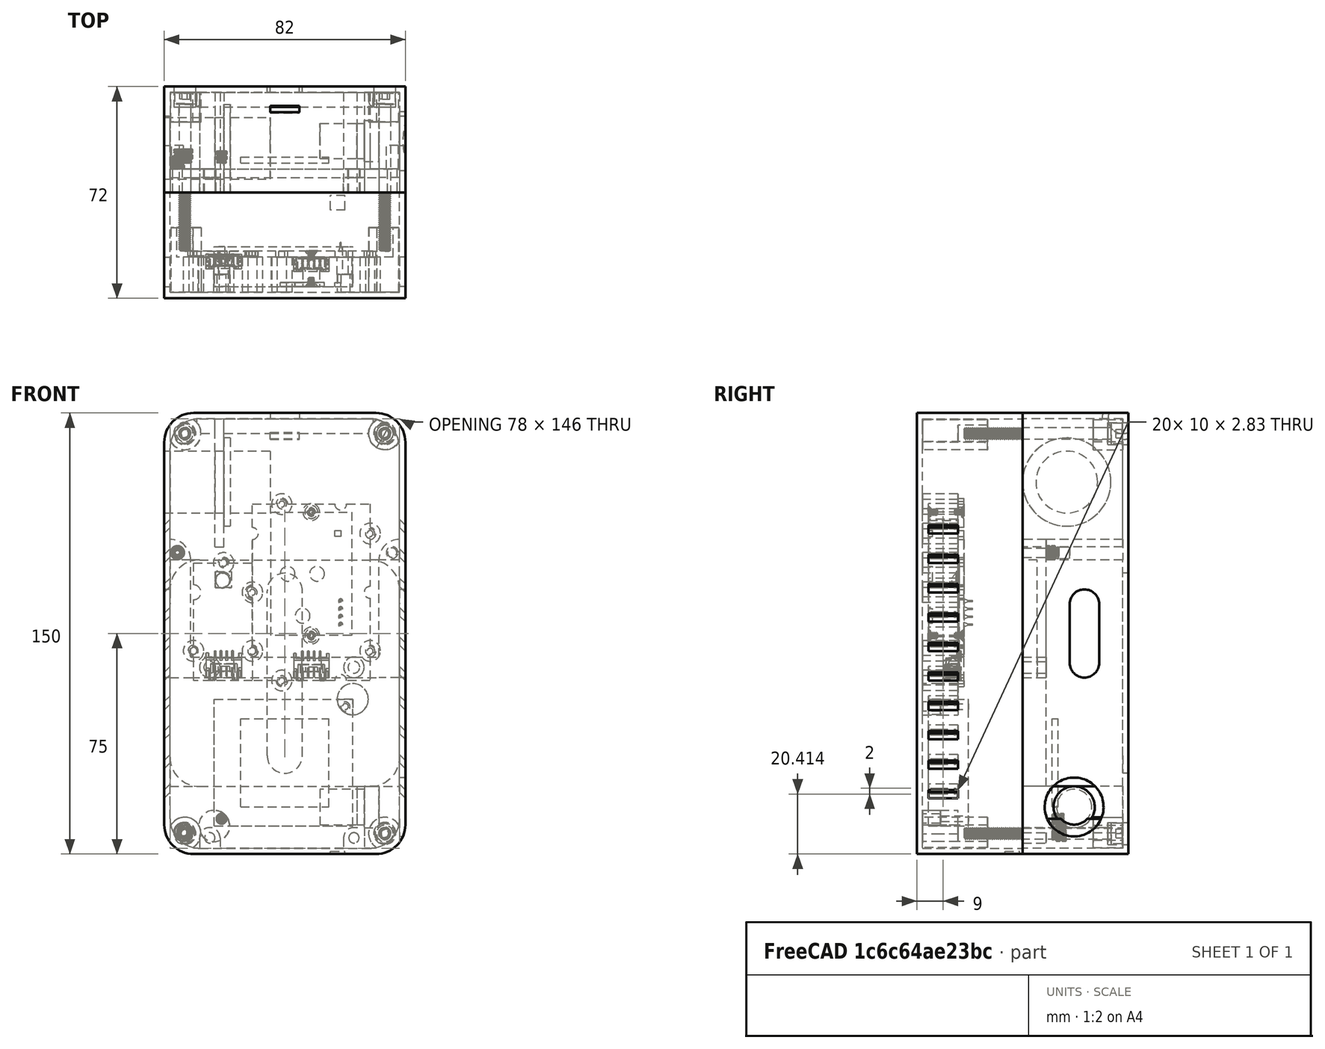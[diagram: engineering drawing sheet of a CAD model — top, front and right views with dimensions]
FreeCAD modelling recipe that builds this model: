
FCSTD DOCUMENT  (FreeCAD 0.20R29177 +233 (Git))
Label: wearableCad_10_11_2022
License: All rights reserved
LicenseURL: http://en.wikipedia.org/wiki/All_rights_reserved
objects: Part::Cylinder×103, Part::Box×65, Part::Cut×53, Part::MultiFuse×39, Part::Feature×10, Part::FeaturePython×1, Mesh::Feature×1
note: 271 computed .brp shape members not serialized (recipe doc carries the construction recipe); baked Part::Feature solids carry a one-line shape summary decoded from their .brp

FEATURE [Part::Feature] Feature  label="Odroid-C4"
  Placement = pos=(66,-10,0) rot=(0.57735,-0.57735,0.57735;2.0944rad)
  shape: bbox 57.1 x 20.65 x 89.5 mm, 2775 faces, 0 solids (baked)
FEATURE [Part::Feature] Feature001  label="SCD30"
  Placement = pos=(-1.3e-14,-22,57) rot=(0,-1,0;1.5708rad)
  shape: bbox 44 x 15.1 x 64 mm, 422 faces, 13 solids (baked)
FEATURE [Part::Feature] Feature002  label="bme280"
  Placement = pos=(-60,-20,58) rot=(0.707107,0,0.707107;3.14159rad)
  shape: bbox 23.8 x 6.016 x 41.9 mm, 221 faces, 2 solids (baked)
FEATURE [Part::MultiFuse] Fusion  label="i2cSensors"
  Placement = pos=(68,-10,0) rot=(0,0,1;0rad)
  Shapes = -> [Feature001,Feature002]
FEATURE [Part::Box] Box  label="ips7100"
  AttacherType = Attacher::AttachEngine3D
  Height = 43.1
  Length = 47.1
  Width = 13.55
FEATURE [Part::Cylinder] Cylinder
  Angle = 360
  AttacherType = Attacher::AttachEngine3D
  FirstAngle = 0
  Height = 13.55
  Placement = pos=(2.5,13.55,2.5) rot=(1,0,0;1.5708rad)
  Radius = 1
  SecondAngle = 0
FEATURE [Part::Cylinder] Cylinder001  label="semiCut"
  Angle = 90
  AttacherType = Attacher::AttachEngine3D
  FirstAngle = 0
  Height = 4.13
  Placement = pos=(0,4.13,-9e-16) rot=(1,0,0;1.5708rad)
  Radius = 5.25
  SecondAngle = 0
FEATURE [Part::MultiFuse] Fusion001  label="ipsCut"
  Shapes = -> [Cylinder,Cylinder001]
FEATURE [Part::Cylinder] Cylinder002
  Angle = 360
  AttacherType = Attacher::AttachEngine3D
  FirstAngle = 0
  Height = 13.55
  Placement = pos=(2.5,13.55,2.5) rot=(1,0,0;1.5708rad)
  Radius = 1
  SecondAngle = 0
FEATURE [Part::Cylinder] Cylinder003  label="semiCut001"
  Angle = 90
  AttacherType = Attacher::AttachEngine3D
  FirstAngle = 0
  Height = 4.13
  Placement = pos=(0,4.13,-9e-16) rot=(1,0,0;1.5708rad)
  Radius = 5.25
  SecondAngle = 0
FEATURE [Part::MultiFuse] Fusion002  label="ipsCut001"
  Placement = pos=(47.1,0,43.1) rot=(0,1,0;3.14159rad)
  Shapes = -> [Cylinder002,Cylinder003]
FEATURE [Part::MultiFuse] Fusion003
  Shapes = -> [Fusion001,Fusion002]
FEATURE [Part::Cut] Cut  label="ips7100V"
  Base = -> Box
  Placement = pos=(15,-42,7.55) rot=(0,0,1;0rad)
  Tool = -> Fusion003
FEATURE [Part::Box] Box001  label="V25B"
  AttacherType = Attacher::AttachEngine3D
  Height = 77
  Length = 78
  Width = 26
FEATURE [Part::Cylinder] Cylinder004
  Angle = 90
  AttacherType = Attacher::AttachEngine3D
  FirstAngle = 0
  Height = 26
  Placement = pos=(0,26,-5.8e-15) rot=(1,0,0;1.5708rad)
  Radius = 10
  SecondAngle = 0
FEATURE [Part::Box] Box002  label="Cube"
  AttacherType = Attacher::AttachEngine3D
  Height = 10
  Length = 10
  Width = 26
FEATURE [Part::Cut] Cut001
  Base = -> Box002
  Placement = pos=(68,0,67) rot=(0,0,1;0rad)
  Tool = -> Cylinder004
FEATURE [Part::Box] Box003  label="Cube001"
  AttacherType = Attacher::AttachEngine3D
  Height = 10
  Length = 10
  Width = 26
FEATURE [Part::Cylinder] Cylinder005
  Angle = 90
  AttacherType = Attacher::AttachEngine3D
  FirstAngle = 0
  Height = 26
  Placement = pos=(0,26,-5.8e-15) rot=(1,0,0;1.5708rad)
  Radius = 10
  SecondAngle = 0
FEATURE [Part::Cut] Cut002
  Base = -> Box003
  Placement = pos=(68,0,10) rot=(0,1,0;1.5708rad)
  Tool = -> Cylinder005
FEATURE [Part::Box] Box004  label="Cube002"
  AttacherType = Attacher::AttachEngine3D
  Height = 10
  Length = 10
  Width = 26
FEATURE [Part::Cylinder] Cylinder006
  Angle = 90
  AttacherType = Attacher::AttachEngine3D
  FirstAngle = 0
  Height = 26
  Placement = pos=(0,26,-5.8e-15) rot=(1,0,0;1.5708rad)
  Radius = 10
  SecondAngle = 0
FEATURE [Part::Cut] Cut003
  Base = -> Box004
  Placement = pos=(10,0,10) rot=(0,1,0;3.14159rad)
  Tool = -> Cylinder006
FEATURE [Part::Box] Box005  label="Cube003"
  AttacherType = Attacher::AttachEngine3D
  Height = 10
  Length = 10
  Width = 26
FEATURE [Part::Cylinder] Cylinder007
  Angle = 90
  AttacherType = Attacher::AttachEngine3D
  FirstAngle = 0
  Height = 26
  Placement = pos=(0,26,-5.8e-15) rot=(1,0,0;1.5708rad)
  Radius = 10
  SecondAngle = 0
FEATURE [Part::Cut] Cut004
  Base = -> Box005
  Placement = pos=(10,0,67) rot=(0,-1,0;1.5708rad)
  Tool = -> Cylinder007
FEATURE [Part::MultiFuse] Fusion004  label="v25Cuts"
  Shapes = -> [Cut001,Cut002,Cut003,Cut004]
FEATURE [Part::Cut] Cut005  label="V25B001"
  Base = -> Box001
  Placement = pos=(0,-2,21) rot=(0,0,1;0rad)
  Tool = -> Fusion004
FEATURE [Part::Box] Box007  label="Cube004"
  AttacherType = Attacher::AttachEngine3D
  Height = 10
  Length = 10
  Placement = pos=(0,-10,0) rot=(0,0,1;0rad)
  Width = 36
FEATURE [Part::Cylinder] Cylinder008
  Angle = 90
  AttacherType = Attacher::AttachEngine3D
  FirstAngle = 0
  Height = 36
  Placement = pos=(0,26,-5.8e-15) rot=(1,0,0;1.5708rad)
  Radius = 10
  SecondAngle = 0
FEATURE [Part::Cut] Cut006
  Base = -> Box007
  Placement = pos=(8,18,8) rot=(0.707107,0,-0.707107;3.14159rad)
  Tool = -> Cylinder008
FEATURE [Part::Box] Box008  label="baseOut001"
  AttacherType = Attacher::AttachEngine3D
  Height = 150
  Length = 82
  Placement = pos=(80,26,-2) rot=(0,0,1;3.14159rad)
  Width = 36
FEATURE [Part::Box] Box009  label="Cube005"
  AttacherType = Attacher::AttachEngine3D
  Height = 10
  Length = 10
  Placement = pos=(0,-10,0) rot=(0,0,1;0rad)
  Width = 36
FEATURE [Part::Cylinder] Cylinder009
  Angle = 90
  AttacherType = Attacher::AttachEngine3D
  FirstAngle = 0
  Height = 36
  Placement = pos=(0,26,-5.8e-15) rot=(1,0,0;1.5708rad)
  Radius = 10
  SecondAngle = 0
FEATURE [Part::Cut] Cut007
  Base = -> Box009
  Placement = pos=(70,18,8) rot=(1,0,0;3.14159rad)
  Tool = -> Cylinder009
FEATURE [Part::Box] Box010  label="Cube006"
  AttacherType = Attacher::AttachEngine3D
  Height = 10
  Length = 10
  Placement = pos=(0,-10,0) rot=(0,0,1;0rad)
  Width = 36
FEATURE [Part::Cylinder] Cylinder010
  Angle = 90
  AttacherType = Attacher::AttachEngine3D
  FirstAngle = 0
  Height = 36
  Placement = pos=(0,26,-5.8e-15) rot=(1,0,0;1.5708rad)
  Radius = 10
  SecondAngle = 0
FEATURE [Part::Cut] Cut008
  Base = -> Box010
  Placement = pos=(8,18,138) rot=(0,0,1;3.14159rad)
  Tool = -> Cylinder010
FEATURE [Part::Box] Box011  label="Cube007"
  AttacherType = Attacher::AttachEngine3D
  Height = 10
  Length = 10
  Placement = pos=(0,-10,0) rot=(0,0,1;0rad)
  Width = 36
FEATURE [Part::Cylinder] Cylinder011
  Angle = 90
  AttacherType = Attacher::AttachEngine3D
  FirstAngle = 0
  Height = 36
  Placement = pos=(0,26,-5.8e-15) rot=(1,0,0;1.5708rad)
  Radius = 10
  SecondAngle = 0
FEATURE [Part::Cut] Cut009
  Base = -> Box011
  Placement = pos=(70,18,138) rot=(0.707107,0,0.707107;3.14159rad)
  Tool = -> Cylinder011
FEATURE [Part::MultiFuse] Fusion005
  Placement = pos=(0,-2,0) rot=(0,0,1;0rad)
  Shapes = -> [Cut006,Cut007,Cut008,Cut009]
FEATURE [Part::Cut] Cut010  label="BaseOut"
  Base = -> Box008
  Tool = -> Fusion005
FEATURE [Part::Box] Box013  label="Cube009"
  AttacherType = Attacher::AttachEngine3D
  Height = 10
  Length = 10
  Placement = pos=(0,-8,0) rot=(0,0,1;0rad)
  Width = 34
FEATURE [Part::Box] Box014  label="baseOut002"
  AttacherType = Attacher::AttachEngine3D
  Height = 146
  Length = 78
  Placement = pos=(80,26,-2) rot=(0,0,1;3.14159rad)
  Width = 34
FEATURE [Part::Box] Box015  label="Cube010"
  AttacherType = Attacher::AttachEngine3D
  Height = 10
  Length = 10
  Placement = pos=(0,-8,0) rot=(0,0,1;0rad)
  Width = 34
FEATURE [Part::Box] Box016  label="Cube011"
  AttacherType = Attacher::AttachEngine3D
  Height = 10
  Length = 10
  Placement = pos=(0,-8,0) rot=(0,0,1;0rad)
  Width = 34
FEATURE [Part::Box] Box017  label="Cube012"
  AttacherType = Attacher::AttachEngine3D
  Height = 10
  Length = 10
  Placement = pos=(0,-8,0) rot=(0,0,1;0rad)
  Width = 34
FEATURE [Part::Cylinder] Cylinder013
  Angle = 90
  AttacherType = Attacher::AttachEngine3D
  FirstAngle = 0
  Height = 34
  Placement = pos=(0,26,-5.8e-15) rot=(1,0,0;1.5708rad)
  Radius = 10
  SecondAngle = 0
FEATURE [Part::Cut] Cut012
  Base = -> Box013
  Placement = pos=(12,18,8) rot=(0.707107,0,-0.707107;3.14159rad)
  Tool = -> Cylinder013
FEATURE [Part::Cylinder] Cylinder014
  Angle = 90
  AttacherType = Attacher::AttachEngine3D
  FirstAngle = 0
  Height = 34
  Placement = pos=(0,26,-5.8e-15) rot=(1,0,0;1.5708rad)
  Radius = 10
  SecondAngle = 0
FEATURE [Part::Cut] Cut013
  Base = -> Box015
  Placement = pos=(70,18,8) rot=(1,0,0;3.14159rad)
  Tool = -> Cylinder014
FEATURE [Part::Cylinder] Cylinder015
  Angle = 90
  AttacherType = Attacher::AttachEngine3D
  FirstAngle = 0
  Height = 34
  Placement = pos=(0,26,-5.8e-15) rot=(1,0,0;1.5708rad)
  Radius = 10
  SecondAngle = 0
FEATURE [Part::Cut] Cut014
  Base = -> Box016
  Placement = pos=(12,18,134) rot=(0,0,1;3.14159rad)
  Tool = -> Cylinder015
FEATURE [Part::Cylinder] Cylinder016
  Angle = 90
  AttacherType = Attacher::AttachEngine3D
  FirstAngle = 0
  Height = 34
  Placement = pos=(0,26,-5.8e-15) rot=(1,0,0;1.5708rad)
  Radius = 10
  SecondAngle = 0
FEATURE [Part::Cut] Cut015
  Base = -> Box017
  Placement = pos=(70,18,134) rot=(0.707107,0,0.707107;3.14159rad)
  Tool = -> Cylinder016
FEATURE [Part::MultiFuse] Fusion006
  Shapes = -> [Cut012,Cut013,Cut014,Cut015]
FEATURE [Part::Cut] Cut016  label="BaseOut001"
  Base = -> Box014
  Placement = pos=(-2,-2,2) rot=(0,0,1;0rad)
  Tool = -> Fusion006
FEATURE [Part::Cut] Cut017  label="baseOut"
  Base = -> Cut010
  Tool = -> Cut016
FEATURE [Part::Box] Box018  label="Cube013"
  AttacherType = Attacher::AttachEngine3D
  Height = 10
  Length = 10
  Placement = pos=(10,26,0) rot=(0,0,1;3.14159rad)
  Width = 26
FEATURE [Part::Cylinder] Cylinder017
  Angle = 90
  AttacherType = Attacher::AttachEngine3D
  FirstAngle = 0
  Height = 26
  Placement = pos=(0,26,-5.8e-15) rot=(1,0,0;1.5708rad)
  Radius = 10
  SecondAngle = 0
FEATURE [Part::Cut] Cut018  label="batterySupport"
  Base = -> Box018
  Placement = pos=(10,-2,31) rot=(0,1,0;3.14159rad)
  Tool = -> Cylinder017
FEATURE [Part::Box] Box019  label="Cube014"
  AttacherType = Attacher::AttachEngine3D
  Height = 10
  Length = 10
  Placement = pos=(10,26,0) rot=(0,0,1;3.14159rad)
  Width = 26
FEATURE [Part::Cylinder] Cylinder018
  Angle = 90
  AttacherType = Attacher::AttachEngine3D
  FirstAngle = 0
  Height = 26
  Placement = pos=(0,26,-5.8e-15) rot=(1,0,0;1.5708rad)
  Radius = 10
  SecondAngle = 0
FEATURE [Part::Cut] Cut019  label="batterySupport001"
  Base = -> Box019
  Placement = pos=(68,-2,31) rot=(0,1,0;1.5708rad)
  Tool = -> Cylinder018
FEATURE [Part::Box] Box020  label="Cube015"
  AttacherType = Attacher::AttachEngine3D
  Height = 10
  Length = 10
  Placement = pos=(10,26,0) rot=(0,0,1;3.14159rad)
  Width = 26
FEATURE [Part::Cylinder] Cylinder019
  Angle = 90
  AttacherType = Attacher::AttachEngine3D
  FirstAngle = 0
  Height = 26
  Placement = pos=(0,26,-5.8e-15) rot=(1,0,0;1.5708rad)
  Radius = 10
  SecondAngle = 0
FEATURE [Part::Cut] Cut020  label="batterySupport002"
  Base = -> Box020
  Placement = pos=(68,-2,88) rot=(0,0,1;0rad)
  Tool = -> Cylinder019
FEATURE [Part::Box] Box021  label="Cube016"
  AttacherType = Attacher::AttachEngine3D
  Height = 10
  Length = 10
  Placement = pos=(10,26,0) rot=(0,0,1;3.14159rad)
  Width = 26
FEATURE [Part::Cylinder] Cylinder020
  Angle = 90
  AttacherType = Attacher::AttachEngine3D
  FirstAngle = 0
  Height = 26
  Placement = pos=(0,26,-5.8e-15) rot=(1,0,0;1.5708rad)
  Radius = 10
  SecondAngle = 0
FEATURE [Part::Cut] Cut021  label="batterySupport003"
  Base = -> Box021
  Placement = pos=(10,-2,88) rot=(0,-1,0;1.5708rad)
  Tool = -> Cylinder020
FEATURE [Part::Cylinder] Cylinder021
  Angle = 360
  AttacherType = Attacher::AttachEngine3D
  FirstAngle = 0
  Height = 34
  Placement = pos=(13.5,24,3.5) rot=(1,0,0;1.5708rad)
  Radius = 3.5
  SecondAngle = 0
FEATURE [Part::Cylinder] Cylinder022
  Angle = 360
  AttacherType = Attacher::AttachEngine3D
  FirstAngle = 0
  Height = 8
  Placement = pos=(13.5,-2,3.5) rot=(1,0,0;1.5708rad)
  Radius = 1.75
  SecondAngle = 0
FEATURE [Part::Box] Box022  label="Cube017"
  AttacherType = Attacher::AttachEngine3D
  Height = 3.5
  Length = 7
  Placement = pos=(10,24,3.5) rot=(1,0,0;3.14159rad)
  Width = 34
FEATURE [Part::Cylinder] Cylinder023
  Angle = 360
  AttacherType = Attacher::AttachEngine3D
  FirstAngle = 0
  Height = 34
  Placement = pos=(62.5,24,3.5) rot=(1,0,0;1.5708rad)
  Radius = 3.5
  SecondAngle = 0
FEATURE [Part::Cylinder] Cylinder024
  Angle = 360
  AttacherType = Attacher::AttachEngine3D
  FirstAngle = 0
  Height = 8
  Placement = pos=(62.5,-2,3.5) rot=(1,0,0;1.5708rad)
  Radius = 1.75
  SecondAngle = 0
FEATURE [Part::Box] Box023  label="Cube018"
  AttacherType = Attacher::AttachEngine3D
  Height = 3.5
  Length = 7
  Placement = pos=(59,24,3.5) rot=(1,0,0;3.14159rad)
  Width = 34
FEATURE [Part::Cylinder] Cylinder025
  Angle = 360
  AttacherType = Attacher::AttachEngine3D
  FirstAngle = 0
  Height = 20
  Radius = 6
  SecondAngle = 0
FEATURE [Part::Cylinder] Cylinder026
  Angle = 360
  AttacherType = Attacher::AttachEngine3D
  FirstAngle = 0
  Height = 5
  Radius = 7
  SecondAngle = 0
FEATURE [Part::MultiFuse] Fusion007  label="powerSwitch"
  Placement = pos=(71,7.5,14) rot=(0,-1,0;1.5708rad)
  Shapes = -> [Cylinder025,Cylinder026]
FEATURE [Part::Box] Box024  label="Cube019"
  AttacherType = Attacher::AttachEngine3D
  Height = 17.5
  Length = 2.5
  Placement = pos=(63.5,24,21) rot=(1,0,0;3.14159rad)
  Width = 34
FEATURE [Part::MultiFuse] Fusion008  label="base"
  Shapes = -> [Cut017,Cut018,Cut019,Cut020,Cut021]
FEATURE [Part::MultiFuse] Fusion009  label="base001"
  Shapes = -> [Cylinder021,Cylinder023,Box022,Box023,Box024,Fusion008]
FEATURE [Part::MultiFuse] Fusion010  label="baseCuts"
  Shapes = -> [Cylinder024,Cylinder022,Fusion007]
FEATURE [Part::Cut] Cut022  label="base002"
  Base = -> Fusion009
  Tool = -> Fusion010
FEATURE [Part::Cylinder] Cylinder027  label="mainMounts"
  Angle = 90
  AttacherType = Attacher::AttachEngine3D
  FirstAngle = 0
  Height = 26
  Placement = pos=(0,24,98) rot=(1,0,0;1.5708rad)
  Radius = 7
  SecondAngle = 0
FEATURE [Part::Cylinder] Cylinder028  label="mainMounts001"
  Angle = 90
  AttacherType = Attacher::AttachEngine3D
  FirstAngle = 0
  Height = 26
  Placement = pos=(78,24,98) rot=(0.57735,-0.57735,0.57735;2.0944rad)
  Radius = 7
  SecondAngle = 0
FEATURE [Part::Cylinder] Cylinder029
  Angle = 360
  AttacherType = Attacher::AttachEngine3D
  FirstAngle = 0
  Height = 8
  Placement = pos=(2.5,-2,100.5) rot=(1,0,0;1.5708rad)
  Radius = 2
  SecondAngle = 0
FEATURE [Part::Cylinder] Cylinder030
  Angle = 360
  AttacherType = Attacher::AttachEngine3D
  FirstAngle = 0
  Height = 8
  Placement = pos=(75.5,-2,100.5) rot=(1,0,0;1.5708rad)
  Radius = 2
  SecondAngle = 0
FEATURE [Part::MultiFuse] Fusion011  label="baseCuts001"
  Placement = pos=(0,8,0) rot=(0,0,1;0rad)
  Shapes = -> [Cylinder029,Cylinder030]
FEATURE [Part::MultiFuse] Fusion012
  Shapes = -> [Cylinder028,Cylinder027]
FEATURE [Part::MultiFuse] Fusion013  label="base003"
  Shapes = -> [Cut022,Fusion012]
FEATURE [Part::Cut] Cut023  label="baseBottom"
  Base = -> Fusion013
  Tool = -> Fusion011
FEATURE [Part::Feature] Solid  label="m3HeatSet"
  Placement = pos=(2.5,2.3,100.5) rot=(1,0,0;3.14159rad)
  shape: bbox 4.772 x 4.354 x 4.772 mm, 239 faces (baked)
FEATURE [Part::Cylinder] Cylinder031
  Angle = 360
  AttacherType = Attacher::AttachEngine3D
  FirstAngle = 0
  Height = 8
  Placement = pos=(13.5,-2,61.5) rot=(1,0,0;1.5708rad)
  Radius = 3.5
  SecondAngle = 0
FEATURE [Part::Cylinder] Cylinder032  label="cuts"
  Angle = 360
  AttacherType = Attacher::AttachEngine3D
  FirstAngle = 0
  Height = 8
  Placement = pos=(13.5,-2,61.5) rot=(1,0,0;1.5708rad)
  Radius = 2
  SecondAngle = 0
FEATURE [Part::Cylinder] Cylinder034
  Angle = 360
  AttacherType = Attacher::AttachEngine3D
  FirstAngle = 0
  Height = 8
  Placement = pos=(62.5,-2,61.5) rot=(1,0,0;1.5708rad)
  Radius = 3.5
  SecondAngle = 0
FEATURE [Part::Cylinder] Cylinder035  label="cuts001"
  Angle = 360
  AttacherType = Attacher::AttachEngine3D
  FirstAngle = 0
  Height = 8
  Placement = pos=(62.5,-2,61.5) rot=(1,0,0;1.5708rad)
  Radius = 2
  SecondAngle = 0
FEATURE [Part::Cylinder] Cylinder036
  Angle = 90
  AttacherType = Attacher::AttachEngine3D
  FirstAngle = 0
  Height = 8
  Placement = pos=(78,-2,98) rot=(0.57735,-0.57735,0.57735;2.0944rad)
  Radius = 7
  SecondAngle = 0
FEATURE [Part::Cylinder] Cylinder037
  Angle = 90
  AttacherType = Attacher::AttachEngine3D
  FirstAngle = 0
  Height = 8
  Placement = pos=(0,-2,98) rot=(1,0,0;1.5708rad)
  Radius = 7
  SecondAngle = 0
FEATURE [Part::Box] Box025  label="Cube020"
  AttacherType = Attacher::AttachEngine3D
  Height = 7
  Length = 78
  Placement = pos=(0,-5,58) rot=(0,0,1;0rad)
  Width = 3
FEATURE [Part::Box] Box026  label="Cube021"
  AttacherType = Attacher::AttachEngine3D
  Height = 7
  Length = 40
  Placement = pos=(7,-5,58) rot=(0,-1,0;1.5708rad)
  Width = 3
FEATURE [Part::Box] Box027  label="Cube022"
  AttacherType = Attacher::AttachEngine3D
  Height = 7
  Length = 40
  Placement = pos=(78,-5,58) rot=(0,-1,0;1.5708rad)
  Width = 3
FEATURE [Part::MultiFuse] Fusion014
  Shapes = -> [Box027,Box025,Box026,Cylinder034,Cylinder031]
FEATURE [Part::Cylinder] Cylinder038  label="m3Screw"
  Angle = 360
  AttacherType = Attacher::AttachEngine3D
  FirstAngle = 0
  Height = 8
  Placement = pos=(75.5,-2,100.5) rot=(1,0,0;1.5708rad)
  Radius = 1.6
  SecondAngle = 0
FEATURE [Part::Cylinder] Cylinder039  label="m3Screw001"
  Angle = 360
  AttacherType = Attacher::AttachEngine3D
  FirstAngle = 0
  Height = 8
  Placement = pos=(2.5,-2,100.5) rot=(1,0,0;1.5708rad)
  Radius = 1.6
  SecondAngle = 0
FEATURE [Part::MultiFuse] Fusion015  label="c4Hold"
  Shapes = -> [Cylinder036,Cylinder037,Fusion014]
FEATURE [Part::MultiFuse] Fusion016  label="c4oldCuts"
  Shapes = -> [Cylinder039,Cylinder032,Cylinder035,Cylinder038]
FEATURE [Part::Cut] Cut024  label="c4Hold001"
  Base = -> Fusion015
  Tool = -> Fusion016
FEATURE [Part::Box] Box028  label="Cube023"
  AttacherType = Attacher::AttachEngine3D
  Height = 10
  Length = 10
  Placement = pos=(0,-10,0) rot=(0,0,1;0rad)
  Width = 36
FEATURE [Part::Box] Box029  label="baseOut003"
  AttacherType = Attacher::AttachEngine3D
  Height = 150
  Length = 82
  Placement = pos=(80,26,-2) rot=(0,0,1;3.14159rad)
  Width = 36
FEATURE [Part::Box] Box030  label="Cube024"
  AttacherType = Attacher::AttachEngine3D
  Height = 10
  Length = 10
  Placement = pos=(0,-10,0) rot=(0,0,1;0rad)
  Width = 36
FEATURE [Part::Box] Box031  label="Cube025"
  AttacherType = Attacher::AttachEngine3D
  Height = 10
  Length = 10
  Placement = pos=(0,-10,0) rot=(0,0,1;0rad)
  Width = 36
FEATURE [Part::Box] Box032  label="Cube026"
  AttacherType = Attacher::AttachEngine3D
  Height = 10
  Length = 10
  Placement = pos=(0,-10,0) rot=(0,0,1;0rad)
  Width = 36
FEATURE [Part::Box] Box033  label="Cube027"
  AttacherType = Attacher::AttachEngine3D
  Height = 10
  Length = 10
  Placement = pos=(0,-8,0) rot=(0,0,1;0rad)
  Width = 34
FEATURE [Part::Box] Box034  label="baseOut004"
  AttacherType = Attacher::AttachEngine3D
  Height = 146
  Length = 78
  Placement = pos=(80,26,-2) rot=(0,0,1;3.14159rad)
  Width = 34
FEATURE [Part::Box] Box035  label="Cube028"
  AttacherType = Attacher::AttachEngine3D
  Height = 10
  Length = 10
  Placement = pos=(0,-8,0) rot=(0,0,1;0rad)
  Width = 34
FEATURE [Part::Box] Box036  label="Cube029"
  AttacherType = Attacher::AttachEngine3D
  Height = 10
  Length = 10
  Placement = pos=(0,-8,0) rot=(0,0,1;0rad)
  Width = 34
FEATURE [Part::Box] Box037  label="Cube030"
  AttacherType = Attacher::AttachEngine3D
  Height = 10
  Length = 10
  Placement = pos=(0,-8,0) rot=(0,0,1;0rad)
  Width = 34
FEATURE [Part::Cylinder] Cylinder040
  Angle = 90
  AttacherType = Attacher::AttachEngine3D
  FirstAngle = 0
  Height = 36
  Placement = pos=(0,26,-5.8e-15) rot=(1,0,0;1.5708rad)
  Radius = 10
  SecondAngle = 0
FEATURE [Part::Cut] Cut025
  Base = -> Box028
  Placement = pos=(8,18,8) rot=(0.707107,0,-0.707107;3.14159rad)
  Tool = -> Cylinder040
FEATURE [Part::Cylinder] Cylinder041
  Angle = 90
  AttacherType = Attacher::AttachEngine3D
  FirstAngle = 0
  Height = 36
  Placement = pos=(0,26,-5.8e-15) rot=(1,0,0;1.5708rad)
  Radius = 10
  SecondAngle = 0
FEATURE [Part::Cut] Cut026
  Base = -> Box030
  Placement = pos=(70,18,8) rot=(1,0,0;3.14159rad)
  Tool = -> Cylinder041
FEATURE [Part::Cylinder] Cylinder042
  Angle = 90
  AttacherType = Attacher::AttachEngine3D
  FirstAngle = 0
  Height = 36
  Placement = pos=(0,26,-5.8e-15) rot=(1,0,0;1.5708rad)
  Radius = 10
  SecondAngle = 0
FEATURE [Part::Cut] Cut027
  Base = -> Box031
  Placement = pos=(8,18,138) rot=(0,0,1;3.14159rad)
  Tool = -> Cylinder042
FEATURE [Part::Cylinder] Cylinder043
  Angle = 90
  AttacherType = Attacher::AttachEngine3D
  FirstAngle = 0
  Height = 36
  Placement = pos=(0,26,-5.8e-15) rot=(1,0,0;1.5708rad)
  Radius = 10
  SecondAngle = 0
FEATURE [Part::Cut] Cut028
  Base = -> Box032
  Placement = pos=(70,18,138) rot=(0.707107,0,0.707107;3.14159rad)
  Tool = -> Cylinder043
FEATURE [Part::Cylinder] Cylinder044
  Angle = 90
  AttacherType = Attacher::AttachEngine3D
  FirstAngle = 0
  Height = 34
  Placement = pos=(0,26,-5.8e-15) rot=(1,0,0;1.5708rad)
  Radius = 10
  SecondAngle = 0
FEATURE [Part::Cut] Cut030
  Base = -> Box033
  Placement = pos=(12,18,8) rot=(0.707107,0,-0.707107;3.14159rad)
  Tool = -> Cylinder044
FEATURE [Part::Cylinder] Cylinder045
  Angle = 90
  AttacherType = Attacher::AttachEngine3D
  FirstAngle = 0
  Height = 34
  Placement = pos=(0,26,-5.8e-15) rot=(1,0,0;1.5708rad)
  Radius = 10
  SecondAngle = 0
FEATURE [Part::Cut] Cut031
  Base = -> Box035
  Placement = pos=(70,18,8) rot=(1,0,0;3.14159rad)
  Tool = -> Cylinder045
FEATURE [Part::Cylinder] Cylinder046
  Angle = 90
  AttacherType = Attacher::AttachEngine3D
  FirstAngle = 0
  Height = 34
  Placement = pos=(0,26,-5.8e-15) rot=(1,0,0;1.5708rad)
  Radius = 10
  SecondAngle = 0
FEATURE [Part::Cut] Cut032
  Base = -> Box036
  Placement = pos=(12,18,134) rot=(0,0,1;3.14159rad)
  Tool = -> Cylinder046
FEATURE [Part::Cylinder] Cylinder047
  Angle = 90
  AttacherType = Attacher::AttachEngine3D
  FirstAngle = 0
  Height = 34
  Placement = pos=(0,26,-5.8e-15) rot=(1,0,0;1.5708rad)
  Radius = 10
  SecondAngle = 0
FEATURE [Part::Cut] Cut033
  Base = -> Box037
  Placement = pos=(70,18,134) rot=(0.707107,0,0.707107;3.14159rad)
  Tool = -> Cylinder047
FEATURE [Part::MultiFuse] Fusion017
  Placement = pos=(0,-2,0) rot=(0,0,1;0rad)
  Shapes = -> [Cut025,Cut026,Cut027,Cut028]
FEATURE [Part::Cut] Cut029  label="BaseOut002"
  Base = -> Box029
  Tool = -> Fusion017
FEATURE [Part::MultiFuse] Fusion018
  Shapes = -> [Cut030,Cut031,Cut032,Cut033]
FEATURE [Part::Cut] Cut034  label="BaseOut003"
  Base = -> Box034
  Placement = pos=(-2,-2,2) rot=(0,0,1;0rad)
  Tool = -> Fusion018
FEATURE [Part::Cut] Cut035  label="baseTop"
  Base = -> Cut029
  Placement = pos=(78,-20,0) rot=(0,0,1;3.14159rad)
  Tool = -> Cut034
FEATURE [Part::Feature] Solid001  label="m2HeatSet"
  Placement = pos=(17.5,0,10) rot=(0,0,1;0rad)
  shape: bbox 3.655 x 4.083 x 3.655 mm, 239 faces (baked)
FEATURE [Part::Cylinder] Cylinder048
  Angle = 360
  AttacherType = Attacher::AttachEngine3D
  FirstAngle = 0
  Height = 6
  Placement = pos=(17.5,-44,10.05) rot=(-1,0,0;1.5708rad)
  Radius = 1.57
  SecondAngle = 0
FEATURE [Part::Cylinder] Cylinder049
  Angle = 360
  AttacherType = Attacher::AttachEngine3D
  FirstAngle = 0
  Height = 6
  Placement = pos=(15,-44,7.55) rot=(0.57735,0.57735,0.57735;4.18879rad)
  Radius = 5.3
  SecondAngle = 0
FEATURE [Part::Cylinder] Cylinder050
  Angle = 360
  AttacherType = Attacher::AttachEngine3D
  FirstAngle = 0
  Height = 6
  Placement = pos=(62.1,-44,50.65) rot=(0.57735,-0.57735,-0.57735;4.18879rad)
  Radius = 5.3
  SecondAngle = 0
FEATURE [Part::Cylinder] Cylinder051
  Angle = 360
  AttacherType = Attacher::AttachEngine3D
  FirstAngle = 0
  Height = 6
  Placement = pos=(59.6,-44,48.15) rot=(-1,0,0;1.5708rad)
  Radius = 1.57
  SecondAngle = 0
FEATURE [Part::Cut] Cut036
  Base = -> Cylinder049
  Tool = -> Cylinder048
FEATURE [Part::Cut] Cut037
  Base = -> Cylinder050
  Tool = -> Cylinder051
FEATURE [Part::Cylinder] Cylinder052
  Angle = 270
  AttacherType = Attacher::AttachEngine3D
  FirstAngle = 0
  Height = 6
  Placement = pos=(15,-38,7.55) rot=(-1,0,0;1.5708rad)
  Radius = 5.3
  SecondAngle = 0
FEATURE [Part::Cylinder] Cylinder053
  Angle = 270
  AttacherType = Attacher::AttachEngine3D
  FirstAngle = 0
  Height = 6
  Placement = pos=(62.1,-38,50.65) rot=(0,0.707107,0.707107;3.14159rad)
  Radius = 5.3
  SecondAngle = 0
FEATURE [Part::MultiFuse] Fusion019  label="baseTop001"
  Shapes = -> [Cut036,Cut037,Cylinder052,Cylinder053,Cut035]
FEATURE [Part::Cylinder] Cylinder054  label="m2HeatSet001"
  Angle = 360
  AttacherType = Attacher::AttachEngine3D
  FirstAngle = 0
  Height = 12
  Placement = pos=(8,-44,67.1) rot=(-1,0,0;1.5708rad)
  Radius = 1.6
  SecondAngle = 0
FEATURE [Part::Cylinder] Cylinder055  label="m2HeatSet002"
  Angle = 360
  AttacherType = Attacher::AttachEngine3D
  FirstAngle = 0
  Height = 12
  Placement = pos=(28,-44,67.1) rot=(-1,0,0;1.5708rad)
  Radius = 1.6
  SecondAngle = 0
FEATURE [Part::Cylinder] Cylinder056  label="m2HeatSet003"
  Angle = 360
  AttacherType = Attacher::AttachEngine3D
  FirstAngle = 0
  Height = 12
  Placement = pos=(68,-44,67.1) rot=(-1,0,0;1.5708rad)
  Radius = 1.6
  SecondAngle = 0
FEATURE [Part::Cylinder] Cylinder057  label="m2HeatSet004"
  Angle = 360
  AttacherType = Attacher::AttachEngine3D
  FirstAngle = 0
  Height = 12
  Placement = pos=(18.2,-44,97) rot=(-1,0,0;1.5708rad)
  Radius = 1.6
  SecondAngle = 0
FEATURE [Part::Cylinder] Cylinder058  label="m2HeatSet005"
  Angle = 360
  AttacherType = Attacher::AttachEngine3D
  FirstAngle = 0
  Height = 12
  Placement = pos=(28,-44,87) rot=(-1,0,0;1.5708rad)
  Radius = 1.6
  SecondAngle = 0
FEATURE [Part::Cylinder] Cylinder059  label="m2HeatSet006"
  Angle = 360
  AttacherType = Attacher::AttachEngine3D
  FirstAngle = 0
  Height = 12
  Placement = pos=(38,-44,117) rot=(-1,0,0;1.5708rad)
  Radius = 1.6
  SecondAngle = 0
FEATURE [Part::Cylinder] Cylinder060  label="m2HeatSet007"
  Angle = 360
  AttacherType = Attacher::AttachEngine3D
  FirstAngle = 0
  Height = 12
  Placement = pos=(38,-44,57) rot=(-1,0,0;1.5708rad)
  Radius = 1.6
  SecondAngle = 0
FEATURE [Part::Cylinder] Cylinder061  label="m2HeatSet008"
  Angle = 360
  AttacherType = Attacher::AttachEngine3D
  FirstAngle = 0
  Height = 12
  Placement = pos=(68,-44,107) rot=(-1,0,0;1.5708rad)
  Radius = 1.6
  SecondAngle = 0
FEATURE [Part::Cylinder] Cylinder062  label="m2HeatSetOut"
  Angle = 360
  AttacherType = Attacher::AttachEngine3D
  FirstAngle = 0
  Height = 12
  Placement = pos=(8,-44,67.1) rot=(-1,0,0;1.5708rad)
  Radius = 3.5
  SecondAngle = 0
FEATURE [Part::Cylinder] Cylinder063  label="m2HeatSetOut001"
  Angle = 360
  AttacherType = Attacher::AttachEngine3D
  FirstAngle = 0
  Height = 12
  Placement = pos=(28,-44,67.1) rot=(-1,0,0;1.5708rad)
  Radius = 3.5
  SecondAngle = 0
FEATURE [Part::Cylinder] Cylinder064  label="m2HeatSetOut002"
  Angle = 360
  AttacherType = Attacher::AttachEngine3D
  FirstAngle = 0
  Height = 12
  Placement = pos=(18.2,-44,97) rot=(-1,0,0;1.5708rad)
  Radius = 3.5
  SecondAngle = 0
FEATURE [Part::Cylinder] Cylinder065  label="m2HeatSetOut003"
  Angle = 360
  AttacherType = Attacher::AttachEngine3D
  FirstAngle = 0
  Height = 12
  Placement = pos=(68,-44,67.1) rot=(-1,0,0;1.5708rad)
  Radius = 3.5
  SecondAngle = 0
FEATURE [Part::Cylinder] Cylinder066  label="m2HeatSetOut004"
  Angle = 360
  AttacherType = Attacher::AttachEngine3D
  FirstAngle = 0
  Height = 12
  Placement = pos=(28,-44,87) rot=(-1,0,0;1.5708rad)
  Radius = 3.5
  SecondAngle = 0
FEATURE [Part::Cylinder] Cylinder067  label="m2HeatSetOut005"
  Angle = 360
  AttacherType = Attacher::AttachEngine3D
  FirstAngle = 0
  Height = 12
  Placement = pos=(38,-44,57) rot=(-1,0,0;1.5708rad)
  Radius = 3.5
  SecondAngle = 0
FEATURE [Part::Cylinder] Cylinder068  label="m2HeatSetOut006"
  Angle = 360
  AttacherType = Attacher::AttachEngine3D
  FirstAngle = 0
  Height = 12
  Placement = pos=(68,-44,107) rot=(-1,0,0;1.5708rad)
  Radius = 3.5
  SecondAngle = 0
FEATURE [Part::Cylinder] Cylinder069  label="m2HeatSetOut007"
  Angle = 360
  AttacherType = Attacher::AttachEngine3D
  FirstAngle = 0
  Height = 12
  Placement = pos=(38,-44,117) rot=(-1,0,0;1.5708rad)
  Radius = 3.5
  SecondAngle = 0
FEATURE [Part::MultiFuse] Fusion020  label="baseTop002"
  Shapes = -> [Cylinder069,Cylinder063,Cylinder064,Cylinder065,Cylinder066,Cylinder067,Cylinder068,Fusion019]
FEATURE [Part::MultiFuse] Fusion021  label="m2HeatSetCuts"
  Shapes = -> [Cylinder062,Cylinder054,Cylinder055,Cylinder056,Cylinder057,Cylinder058,Cylinder059,Cylinder060,Cylinder061]
FEATURE [Part::Cut] Cut038  label="baseTop003"
  Base = -> Fusion020
  Tool = -> Fusion021
FEATURE [Part::Cylinder] Cylinder070
  Angle = 360
  AttacherType = Attacher::AttachEngine3D
  FirstAngle = 0
  Height = 20
  Radius = 6
  SecondAngle = 0
FEATURE [Part::Cylinder] Cylinder071
  Angle = 360
  AttacherType = Attacher::AttachEngine3D
  FirstAngle = 0
  Height = 5
  Radius = 7
  SecondAngle = 0
FEATURE [Part::MultiFuse] Fusion022  label="powerSwitch001"
  Placement = pos=(71,7.5,14) rot=(0,-1,0;1.5708rad)
  Shapes = -> [Cylinder070,Cylinder071]
FEATURE [Part::Feature] Solid002  label="M4Screw"
  Placement = pos=(73,-30,5) rot=(0.57735,-0.57735,0.57735;2.0944rad)
  shape: bbox 7.001 x 54.15 x 7.001 mm, 147 faces (baked)
FEATURE [Part::Feature] Solid003  label="M4Screw001"
  Placement = pos=(5,-30,5) rot=(0.57735,-0.57735,0.57735;2.0944rad)
  shape: bbox 7.001 x 54.15 x 7.001 mm, 147 faces (baked)
FEATURE [Part::Feature] Solid004  label="M4Screw002"
  Placement = pos=(5,-30,141) rot=(0.57735,-0.57735,0.57735;2.0944rad)
  shape: bbox 7.001 x 54.15 x 7.001 mm, 147 faces (baked)
FEATURE [Part::Feature] Solid005  label="M4Screw003"
  Placement = pos=(73,-30,141) rot=(0.57735,-0.57735,0.57735;2.0944rad)
  shape: bbox 7.001 x 54.15 x 7.001 mm, 147 faces (baked)
FEATURE [Part::Cylinder] Cylinder072  label="m4HoleBase"
  Angle = 360
  AttacherType = Attacher::AttachEngine3D
  FirstAngle = 0
  Height = 22
  Placement = pos=(4.5,-44,141.5) rot=(0.377964,0.654654,0.654654;3.86433rad)
  Radius = 5.5
  SecondAngle = 0
FEATURE [Part::Cylinder] Cylinder073  label="m4HeatSetCut"
  Angle = 360
  AttacherType = Attacher::AttachEngine3D
  FirstAngle = 0
  Height = 10
  Placement = pos=(4.5,-32,141.5) rot=(-1,0,0;1.5708rad)
  Radius = 2.8
  SecondAngle = 0
FEATURE [Part::Cut] Cut039  label="m4HeatSetHoles"
  Base = -> Cylinder072
  Placement = pos=(0.5,0,-0.5) rot=(0,0,1;0rad)
  Tool = -> Cylinder073
FEATURE [Part::Cylinder] Cylinder074  label="m4HoleBase001"
  Angle = 360
  AttacherType = Attacher::AttachEngine3D
  FirstAngle = 0
  Height = 22
  Placement = pos=(4.5,-44,141.5) rot=(0.38203,0.653473,0.653473;3.86433rad)
  Radius = 5.5
  SecondAngle = 0
FEATURE [Part::Cylinder] Cylinder075  label="m4HeatSetCut001"
  Angle = 360
  AttacherType = Attacher::AttachEngine3D
  FirstAngle = 0
  Height = 10
  Placement = pos=(4.5,-32,141.5) rot=(-1,0,0;1.5708rad)
  Radius = 2.8
  SecondAngle = 0
FEATURE [Part::Cut] Cut040  label="m4HeatSetHoles001"
  Base = -> Cylinder074
  Placement = pos=(68.5,0,-0.5) rot=(0,0,1;0rad)
  Tool = -> Cylinder075
FEATURE [Part::Cylinder] Cylinder076  label="m4HoleBase002"
  Angle = 360
  AttacherType = Attacher::AttachEngine3D
  FirstAngle = 0
  Height = 22
  Placement = pos=(4.5,-44,141.5) rot=(0.377964,0.654654,0.654654;3.86433rad)
  Radius = 5.5
  SecondAngle = 0
FEATURE [Part::Cylinder] Cylinder077  label="m4HeatSetCut002"
  Angle = 360
  AttacherType = Attacher::AttachEngine3D
  FirstAngle = 0
  Height = 10
  Placement = pos=(4.5,-32,141.5) rot=(-1,0,0;1.5708rad)
  Radius = 2.8
  SecondAngle = 0
FEATURE [Part::Cut] Cut041  label="m4HeatSetHoles002"
  Base = -> Cylinder076
  Placement = pos=(0.5,0,-136.5) rot=(0,0,1;0rad)
  Tool = -> Cylinder077
FEATURE [Part::Cylinder] Cylinder078  label="m4HoleBase003"
  Angle = 360
  AttacherType = Attacher::AttachEngine3D
  FirstAngle = 0
  Height = 22
  Placement = pos=(4.5,-44,141.5) rot=(0.377964,0.654654,0.654654;3.86433rad)
  Radius = 5.5
  SecondAngle = 0
FEATURE [Part::Cylinder] Cylinder079  label="m4HeatSetCut003"
  Angle = 360
  AttacherType = Attacher::AttachEngine3D
  FirstAngle = 0
  Height = 10
  Placement = pos=(4.5,-32,141.5) rot=(-1,0,0;1.5708rad)
  Radius = 2.8
  SecondAngle = 0
FEATURE [Part::Cut] Cut042  label="m4HeatSetHoles003"
  Base = -> Cylinder078
  Placement = pos=(68.5,0,-136.5) rot=(0,0,1;0rad)
  Tool = -> Cylinder079
FEATURE [Part::MultiFuse] Fusion023  label="baseTop004"
  Shapes = -> [Cut039,Cut040,Cut041,Cut042,Cut038]
FEATURE [Part::Feature] Solid006  label="m4HeatSet"
  Placement = pos=(4.5,0,5.5) rot=(0,0,1;0rad)
  shape: bbox 6.396 x 4.801 x 6.396 mm, 237 faces (baked)
FEATURE [Part::Cylinder] Cylinder080  label="m2HeatSetOut008"
  Angle = 360
  AttacherType = Attacher::AttachEngine3D
  FirstAngle = 0
  Height = 12
  Placement = pos=(8,-44,67.1) rot=(-1,0,0;1.5708rad)
  Radius = 3.5
  SecondAngle = 0
FEATURE [Part::Cylinder] Cylinder081  label="m2HeatSet009"
  Angle = 360
  AttacherType = Attacher::AttachEngine3D
  FirstAngle = 0
  Height = 12
  Placement = pos=(8,-44,67.1) rot=(-1,0,0;1.5708rad)
  Radius = 1.6
  SecondAngle = 0
FEATURE [Part::Cut] Cut043  label="m2HeatSet010"
  Base = -> Cylinder080
  Tool = -> Cylinder081
FEATURE [Part::MultiFuse] Fusion024  label="baseTop005"
  Shapes = -> [Fusion023,Cut043]
FEATURE [Part::Cylinder] Cylinder084  label="m4HoleBase006"
  Angle = 360
  AttacherType = Attacher::AttachEngine3D
  FirstAngle = 0
  Height = 12
  Placement = pos=(73,26,5) rot=(0,0.707107,-0.707107;3.14159rad)
  Radius = 5.5
  SecondAngle = 0
FEATURE [Part::Cylinder] Cylinder085  label="m4HoleBaseCut"
  Angle = 360
  AttacherType = Attacher::AttachEngine3D
  FirstAngle = 0
  Height = 7
  Placement = pos=(73,26,5) rot=(0,0.707107,-0.707107;3.14159rad)
  Radius = 3.75
  SecondAngle = 0
FEATURE [Part::Cylinder] Cylinder086  label="m4HoleBase007"
  Angle = 360
  AttacherType = Attacher::AttachEngine3D
  FirstAngle = 0
  Height = 12
  Placement = pos=(5,26,5) rot=(0,0.707107,-0.707107;3.14159rad)
  Radius = 5.5
  SecondAngle = 0
FEATURE [Part::Cylinder] Cylinder087  label="m4HoleBaseCut001"
  Angle = 360
  AttacherType = Attacher::AttachEngine3D
  FirstAngle = 0
  Height = 7
  Placement = pos=(5,26,5) rot=(0,0.707107,-0.707107;3.14159rad)
  Radius = 3.75
  SecondAngle = 0
FEATURE [Part::Cylinder] Cylinder088  label="m4HoleBase008"
  Angle = 360
  AttacherType = Attacher::AttachEngine3D
  FirstAngle = 0
  Height = 12
  Placement = pos=(73,26,141) rot=(0,0.707107,-0.707107;3.14159rad)
  Radius = 5.5
  SecondAngle = 0
FEATURE [Part::Cylinder] Cylinder089  label="m4HoleBaseCut002"
  Angle = 360
  AttacherType = Attacher::AttachEngine3D
  FirstAngle = 0
  Height = 7
  Placement = pos=(73,26,141) rot=(0,0.707107,-0.707107;3.14159rad)
  Radius = 3.75
  SecondAngle = 0
FEATURE [Part::Cylinder] Cylinder090  label="m4HoleBase009"
  Angle = 360
  AttacherType = Attacher::AttachEngine3D
  FirstAngle = 0
  Height = 12
  Placement = pos=(5,26,141) rot=(0,0.707107,-0.707107;3.14159rad)
  Radius = 5.5
  SecondAngle = 0
FEATURE [Part::Cylinder] Cylinder091  label="m4HoleBaseCut003"
  Angle = 360
  AttacherType = Attacher::AttachEngine3D
  FirstAngle = 0
  Height = 7
  Placement = pos=(5,26,141) rot=(0,0.707107,-0.707107;3.14159rad)
  Radius = 3.75
  SecondAngle = 0
FEATURE [Part::MultiFuse] Fusion025  label="baseBottom001"
  Shapes = -> [Cylinder084,Cylinder086,Cylinder088,Cylinder090,Cut023]
FEATURE [Part::MultiFuse] Fusion026  label="m4Cuts"
  Shapes = -> [Cylinder085,Cylinder087,Cylinder089,Cylinder091]
FEATURE [Part::Cut] Cut044  label="baseBottom002"
  Base = -> Fusion025
  Tool = -> Fusion026
FEATURE [Part::Cylinder] Cylinder092  label="m4HoleBaseCut004"
  Angle = 360
  AttacherType = Attacher::AttachEngine3D
  FirstAngle = 0
  Height = 7
  Placement = pos=(73,26,5) rot=(0,0.707107,-0.707107;3.14159rad)
  Radius = 2.1
  SecondAngle = 0
FEATURE [Part::Cylinder] Cylinder093  label="m4HoleBaseCut005"
  Angle = 360
  AttacherType = Attacher::AttachEngine3D
  FirstAngle = 0
  Height = 7
  Placement = pos=(5,26,5) rot=(0,0.707107,-0.707107;3.14159rad)
  Radius = 2.1
  SecondAngle = 0
FEATURE [Part::Cylinder] Cylinder094  label="m4HoleBaseCut006"
  Angle = 360
  AttacherType = Attacher::AttachEngine3D
  FirstAngle = 0
  Height = 7
  Placement = pos=(73,26,141) rot=(0,0.707107,-0.707107;3.14159rad)
  Radius = 2.1
  SecondAngle = 0
FEATURE [Part::Cylinder] Cylinder095  label="m4HoleBaseCut007"
  Angle = 360
  AttacherType = Attacher::AttachEngine3D
  FirstAngle = 0
  Height = 7
  Placement = pos=(5,26,141) rot=(0,0.707107,-0.707107;3.14159rad)
  Radius = 2.1
  SecondAngle = 0
FEATURE [Part::MultiFuse] Fusion027  label="m4Cuts001"
  Placement = pos=(0,-5,0) rot=(0,0,1;0rad)
  Shapes = -> [Cylinder092,Cylinder093,Cylinder094,Cylinder095]
FEATURE [Part::Cut] Cut045  label="baseBottom003"
  Base = -> Cut044
  Tool = -> Fusion027
FEATURE [Part::Cylinder] Cylinder096
  Angle = 360
  AttacherType = Attacher::AttachEngine3D
  FirstAngle = 0
  Height = 20
  Radius = 6
  SecondAngle = 0
FEATURE [Part::Cylinder] Cylinder097
  Angle = 360
  AttacherType = Attacher::AttachEngine3D
  FirstAngle = 0
  Height = 5
  Radius = 10
  SecondAngle = 0
FEATURE [Part::MultiFuse] Fusion028  label="Switch"
  Placement = pos=(83,7.5,14) rot=(0,-1,0;1.5708rad)
  Shapes = -> [Cylinder096,Cylinder097]
FEATURE [Part::Cylinder] Cylinder098  label="Ethernet"
  Angle = 360
  AttacherType = Attacher::AttachEngine3D
  FirstAngle = 0
  Height = 36
  Radius = 10.5
  SecondAngle = 0
FEATURE [Part::Cylinder] Cylinder099  label="Ethernet001"
  Angle = 360
  AttacherType = Attacher::AttachEngine3D
  FirstAngle = 0
  Height = 2.25
  Placement = pos=(0,0,13.5) rot=(0,0,1;0rad)
  Radius = 15
  SecondAngle = 0
FEATURE [Part::MultiFuse] Fusion029  label="EthenetCut"
  Placement = pos=(34,5,124.5) rot=(0,-1,0;1.5708rad)
  Shapes = -> [Cylinder098,Cylinder099]
FEATURE [Part::Box] Box038  label="ethernetHold"
  AttacherType = Attacher::AttachEngine3D
  Height = 34
  Length = 3
  Placement = pos=(15.3,24,102.5) rot=(1,0,0;1.5708rad)
  Width = 43.5
FEATURE [Part::Cylinder] Cylinder100  label="Ethernet002"
  Angle = 360
  AttacherType = Attacher::AttachEngine3D
  FirstAngle = 0
  Height = 36
  Radius = 10.5
  SecondAngle = 0
FEATURE [Part::Cylinder] Cylinder101  label="Ethernet003"
  Angle = 360
  AttacherType = Attacher::AttachEngine3D
  FirstAngle = 0
  Height = 2.25
  Placement = pos=(0,0,13.5) rot=(0,0,1;0rad)
  Radius = 15
  SecondAngle = 0
FEATURE [Part::MultiFuse] Fusion030  label="Ethenet001"
  Placement = pos=(34,5,124.5) rot=(0,-1,0;1.5708rad)
  Shapes = -> [Cylinder100,Cylinder101]
FEATURE [Part::MultiFuse] Fusion031  label="baseBottom004"
  Shapes = -> [Cut045,Box038]
FEATURE [Part::Cylinder] Cylinder102  label="hookReinforment"
  Angle = 90
  AttacherType = Attacher::AttachEngine3D
  FirstAngle = 0
  Height = 60
  Placement = pos=(9,24,146) rot=(0.57735,-0.57735,0.57735;4.18879rad)
  Radius = 5
  SecondAngle = 0
FEATURE [Part::FeaturePython] Tube  label="hookCut"  # WARN: FeaturePython — macro-defined, semantics opaque (R4)
  AttacherType = Attacher::AttachEngine3D
  Height = 10
  InnerRadius = 5
  OuterRadius = 7
  Placement = pos=(34,24,146) rot=(0,1,0;1.5708rad)
FEATURE [Part::MultiFuse] Fusion032  label="baseBottom005"
  Shapes = -> [Fusion031,Cylinder102]
FEATURE [Part::MultiFuse] Fusion033  label="baseBottomCuts"
  Shapes = -> [Fusion029,Fusion028,Tube]
FEATURE [Part::Cut] Cut046  label="baseBottom006"
  Base = -> Fusion032
  Tool = -> Fusion033
FEATURE [Part::Box] Box039  label="usbCut"
  AttacherType = Attacher::AttachEngine3D
  Height = 10
  Length = 82
  Width = 30
FEATURE [Part::Cylinder] Cylinder103
  Angle = 180
  AttacherType = Attacher::AttachEngine3D
  FirstAngle = 0
  Height = 82
  Placement = pos=(0,5,5) rot=(0.707107,0,0.707107;3.14159rad)
  Radius = 5
  SecondAngle = 0
FEATURE [Part::Box] Box040  label="Cube032"
  AttacherType = Attacher::AttachEngine3D
  Height = 10
  Length = 82
  Width = 5
FEATURE [Part::Cut] Cut047  label="cornerCuts"
  Base = -> Box040
  Tool = -> Cylinder103
FEATURE [Part::Box] Box041  label="Cube033"
  AttacherType = Attacher::AttachEngine3D
  Height = 10
  Length = 82
  Width = 5
FEATURE [Part::Cylinder] Cylinder104
  Angle = 180
  AttacherType = Attacher::AttachEngine3D
  FirstAngle = 0
  Height = 82
  Placement = pos=(0,5,5) rot=(0.707107,0,0.707107;3.14159rad)
  Radius = 5
  SecondAngle = 0
FEATURE [Part::Cut] Cut048  label="cornerCuts001"
  Base = -> Box041
  Placement = pos=(0,30,10) rot=(1,0,0;3.14159rad)
  Tool = -> Cylinder104
FEATURE [Part::MultiFuse] Fusion034
  Shapes = -> [Cut047,Cut048]
FEATURE [Part::Cut] Cut049  label="usbCut001"
  Base = -> Box039
  Placement = pos=(-2,16,58) rot=(1,0,0;1.5708rad)
  Tool = -> Fusion034
FEATURE [Part::Cut] Cut050  label="baseBottom007"
  Base = -> Cut046
  Tool = -> Cut049
FEATURE [Part::Box] Box042  label="Cube034"
  AttacherType = Attacher::AttachEngine3D
  Height = 56
  Length = 12
  Width = 2
FEATURE [Part::Cylinder] Cylinder105
  Angle = 360
  AttacherType = Attacher::AttachEngine3D
  FirstAngle = 0
  Height = 2
  Placement = pos=(6,0,0) rot=(0,0.707107,0.707107;3.14159rad)
  Radius = 6
  SecondAngle = 0
FEATURE [Part::Cylinder] Cylinder106
  Angle = 360
  AttacherType = Attacher::AttachEngine3D
  FirstAngle = 0
  Height = 2
  Placement = pos=(6,1.2e-14,56) rot=(0,0.707107,0.707107;3.14159rad)
  Radius = 6
  SecondAngle = 0
FEATURE [Part::MultiFuse] Fusion035  label="voltaicCut"
  Placement = pos=(33,24,31.5) rot=(0,0,1;0rad)
  Shapes = -> [Cylinder106,Cylinder105,Box042]
FEATURE [Part::Cut] Cut051  label="baseBottom008"
  Base = -> Cut050
  Tool = -> Fusion035
FEATURE [Part::Box] Box043  label="lightCut"
  AttacherType = Attacher::AttachEngine3D
  Height = 5
  Length = 5
  Placement = pos=(54.5,-16,-6) rot=(0,0,1;0rad)
  Width = 5
FEATURE [Part::Cut] Cut052  label="baseTop006"
  Base = -> Fusion024
  Tool = -> Box043
FEATURE [Part::Box] Box044  label="Cube035"
  AttacherType = Attacher::AttachEngine3D
  Height = 30
  Length = 30
  Placement = pos=(24,0,14) rot=(0,0,1;0rad)
  Width = 2
FEATURE [Part::Box] Box045  label="Cube036"
  AttacherType = Attacher::AttachEngine3D
  Height = 2
  Length = 20
  Placement = pos=(0,0,0) rot=(0,1,0;5.49779rad)
  Width = 10
FEATURE [Part::Box] Box046  label="Cube037"
  AttacherType = Attacher::AttachEngine3D
  Height = 2
  Length = 20
  Placement = pos=(0,0,10) rot=(0,-1,0;0.785398rad)
  Width = 10
FEATURE [Part::Box] Box047  label="Cube038"
  AttacherType = Attacher::AttachEngine3D
  Height = 2
  Length = 20
  Placement = pos=(0,0,20) rot=(0,-1,0;0.785398rad)
  Width = 10
FEATURE [Part::Box] Box048  label="Cube039"
  AttacherType = Attacher::AttachEngine3D
  Height = 2
  Length = 20
  Placement = pos=(0,0,30) rot=(0,-1,0;0.785398rad)
  Width = 10
FEATURE [Part::Box] Box049  label="Cube040"
  AttacherType = Attacher::AttachEngine3D
  Height = 2
  Length = 10
  Placement = pos=(0,0,40) rot=(0,-1,0;0.785398rad)
  Width = 10
FEATURE [Part::Box] Box050  label="Cube041"
  AttacherType = Attacher::AttachEngine3D
  Height = 2
  Length = 20
  Placement = pos=(0,0,50) rot=(0,-1,0;0.785398rad)
  Width = 10
FEATURE [Part::Box] Box051  label="Cube042"
  AttacherType = Attacher::AttachEngine3D
  Height = 2
  Length = 20
  Placement = pos=(0,0,60) rot=(0,-1,0;0.785398rad)
  Width = 10
FEATURE [Part::Box] Box052  label="Cube043"
  AttacherType = Attacher::AttachEngine3D
  Height = 2
  Length = 20
  Placement = pos=(0,0,70) rot=(0,-1,0;0.785398rad)
  Width = 10
FEATURE [Part::Box] Box053  label="Cube044"
  AttacherType = Attacher::AttachEngine3D
  Height = 2
  Length = 20
  Placement = pos=(0,0,80) rot=(0,-1,0;0.785398rad)
  Width = 10
FEATURE [Part::Box] Box054  label="Cube045"
  AttacherType = Attacher::AttachEngine3D
  Height = 2
  Length = 20
  Placement = pos=(0,0,90) rot=(0,-1,0;0.785398rad)
  Width = 10
FEATURE [Part::Box] Box055  label="Cube046"
  AttacherType = Attacher::AttachEngine3D
  Height = 2
  Length = 20
  Placement = pos=(0,0,1000) rot=(0,-1,0;0.785398rad)
  Width = 10
FEATURE [Part::MultiFuse] Fusion036
  Placement = pos=(-4,-10,15) rot=(0,0,1;0rad)
  Shapes = -> [Box045,Box046,Box047,Box048,Box049,Box050,Box051,Box052,Box053,Box054,Box055]
FEATURE [Part::Box] Box056  label="Cube047"
  AttacherType = Attacher::AttachEngine3D
  Height = 2
  Length = 20
  Placement = pos=(0,0,0) rot=(0,-1,0;0.785398rad)
  Width = 10
FEATURE [Part::Box] Box057  label="Cube048"
  AttacherType = Attacher::AttachEngine3D
  Height = 2
  Length = 20
  Placement = pos=(0,0,10) rot=(0,-1,0;0.785398rad)
  Width = 10
FEATURE [Part::Box] Box058  label="Cube049"
  AttacherType = Attacher::AttachEngine3D
  Height = 2
  Length = 20
  Placement = pos=(0,0,20) rot=(0,-1,0;0.785398rad)
  Width = 10
FEATURE [Part::Box] Box059  label="Cube050"
  AttacherType = Attacher::AttachEngine3D
  Height = 2
  Length = 20
  Placement = pos=(0,0,30) rot=(0,-1,0;0.785398rad)
  Width = 10
FEATURE [Part::Box] Box060  label="Cube051"
  AttacherType = Attacher::AttachEngine3D
  Height = 2
  Length = 10
  Placement = pos=(0,0,40) rot=(0,-1,0;0.785398rad)
  Width = 10
FEATURE [Part::Box] Box061  label="Cube052"
  AttacherType = Attacher::AttachEngine3D
  Height = 2
  Length = 20
  Placement = pos=(0,0,50) rot=(0,-1,0;0.785398rad)
  Width = 10
FEATURE [Part::Box] Box062  label="Cube053"
  AttacherType = Attacher::AttachEngine3D
  Height = 2
  Length = 20
  Placement = pos=(0,0,60) rot=(0,-1,0;0.785398rad)
  Width = 10
FEATURE [Part::Box] Box063  label="Cube054"
  AttacherType = Attacher::AttachEngine3D
  Height = 2
  Length = 20
  Placement = pos=(0,0,70) rot=(0,-1,0;0.785398rad)
  Width = 10
FEATURE [Part::Box] Box064  label="Cube055"
  AttacherType = Attacher::AttachEngine3D
  Height = 2
  Length = 10
  Placement = pos=(0,0,80) rot=(0,-1,0;0.785398rad)
  Width = 10
FEATURE [Part::Box] Box065  label="Cube056"
  AttacherType = Attacher::AttachEngine3D
  Height = 2
  Length = 20
  Placement = pos=(0,0,90) rot=(0,-1,0;0.785398rad)
  Width = 10
FEATURE [Part::Box] Box066  label="Cube057"
  AttacherType = Attacher::AttachEngine3D
  Height = 2
  Length = 20
  Placement = pos=(0,0,1000) rot=(0,-1,0;0.785398rad)
  Width = 10
FEATURE [Part::MultiFuse] Fusion037
  Placement = pos=(82,0,15) rot=(0,0,1;3.14159rad)
  Shapes = -> [Box056,Box057,Box058,Box059,Box060,Box061,Box062,Box063,Box064,Box065,Box066]
FEATURE [Part::MultiFuse] Fusion038  label="vents"
  Placement = pos=(0,-32,0) rot=(0,0,1;0rad)
  Shapes = -> [Fusion036,Fusion037]
FEATURE [Part::Cut] Cut053
  Base = -> Cut052
  Tool = -> Fusion038
FEATURE [Mesh::Feature] ImageToStl_com_depositphotos_mint_leaf_scaled_1_768x601_removebg__1_  label="ImageToStl.com_depositphotos_mint-leaf-scaled-1-768x601-removebg-_1_"
